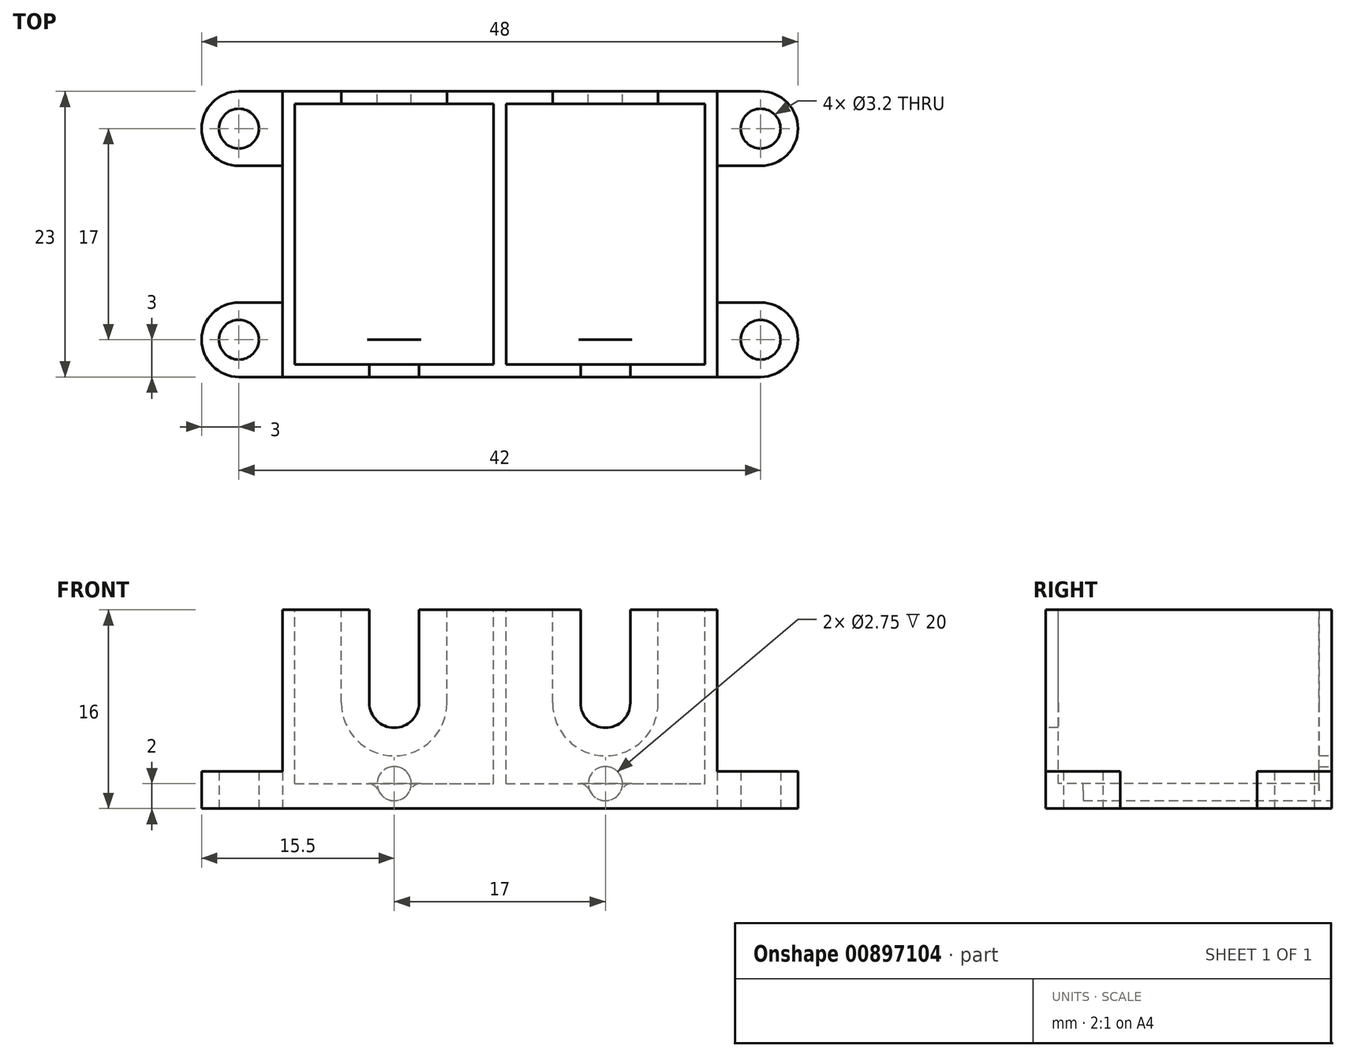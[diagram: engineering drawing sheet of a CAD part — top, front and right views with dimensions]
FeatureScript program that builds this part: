
annotation { "Feature Type Name" : "Feature", "Feature Type Description" : "" }
export const myFeature = defineFeature(function(context is Context, id is Id, definition is map)
    precondition{}
    {
        {
            var Q0;
            Q0=qCreatedBy(makeId("Top.planeOp"),FACE);
            var sketch = newSketch(context, id + "F0", { "sketchPlane" : qUnion([Q0])});
            skLineSegment(sketch, "E0.bottom", {"start": v(-17.5, 11.5) * mm, "end": v(17.5, 11.5) * mm});
            skLineSegment(sketch, "E0.top", {"start": v(-17.5, -11.5) * mm, "end": v(17.5, -11.5) * mm});
            skLineSegment(sketch, "E0.left", {"start": v(-17.5, 11.5) * mm, "end": v(-17.5, -11.5) * mm});
            skLineSegment(sketch, "E0.right", {"start": v(17.5, 11.5) * mm, "end": v(17.5, -11.5) * mm});
            skSolve(sketch);
        }
        {
            var Q0;
            Q0 = qSketchRegion(id + "F0", true);
            extrude(context, id + "F1", {"entities" : qUnion([Q0]), "depth" : 16 * mm, "offsetDistance" : 25 * mm});
        }
        {
            var Q0;
            Q0=makeQuery(id+"F1.opExtrude","CAP_FACE",FACE,{"disambiguationData":[OSD([sQuery(id+"F0.wireOp",EDGE,"E0.bottom"),sQuery(id+"F0.wireOp",EDGE,"E0.top"),sQuery(id+"F0.wireOp",EDGE,"E0.left"),sQuery(id+"F0.wireOp",EDGE,"E0.right")])],"isStart":false});
            var sketch = newSketch(context, id + "F2", { "sketchPlane" : qUnion([Q0])});
            skLineSegment(sketch, "E1.bottom", {"start": v(-16.5, 10.5) * mm, "end": v(-0.5, 10.5) * mm});
            skLineSegment(sketch, "E1.top", {"start": v(-16.5, -10.5) * mm, "end": v(-0.5, -10.5) * mm});
            skLineSegment(sketch, "E1.left", {"start": v(-16.5, 10.5) * mm, "end": v(-16.5, -10.5) * mm});
            skLineSegment(sketch, "E1.right", {"start": v(-0.5, 10.5) * mm, "end": v(-0.5, -10.5) * mm});
            skLineSegment(sketch, "E2.bottom", {"start": v(0.5, 10.5) * mm, "end": v(16.5, 10.5) * mm});
            skLineSegment(sketch, "E2.top", {"start": v(0.5, -10.5) * mm, "end": v(16.5, -10.5) * mm});
            skLineSegment(sketch, "E2.left", {"start": v(0.5, 10.5) * mm, "end": v(0.5, -10.5) * mm});
            skLineSegment(sketch, "E2.right", {"start": v(16.5, 10.5) * mm, "end": v(16.5, -10.5) * mm});
            skSolve(sketch);
        }
        {
            var Q0;
            Q0 = qSketchRegion(id + "F2", true);
            extrude(context, id + "F3", {"entities" : qUnion([Q0]), "operationType" : NewBodyOperationType.REMOVE, "oppositeDirection" : true, "depth" : 14 * mm, "offsetDistance" : 25 * mm});
        }
        {
            var Q0;
            Q0=makeQuery(id+"F1.opExtrude","SWEPT_FACE",FACE,{"disambiguationData":[OSD([sQuery(id+"F0.wireOp",EDGE,"E0.top")])]});
            var sketch = newSketch(context, id + "F4", { "sketchPlane" : qUnion([Q0])});
            skArc(sketch, "E3", {"start": v(-10.5, 8.5) * mm, "mid": v(-8.5, 6.5) * mm, "end": v(-6.5, 8.5) * mm});
            skArc(sketch, "E4", {"start": v(6.5, 8.5) * mm, "mid": v(8.5, 6.5) * mm, "end": v(10.5, 8.5) * mm});
            skLineSegment(sketch, "E5.top", {"start": v(-10.5, 16) * mm, "end": v(-6.5, 16) * mm});
            skLineSegment(sketch, "E5.left", {"start": v(-10.5, 8.5) * mm, "end": v(-10.5, 16) * mm});
            skLineSegment(sketch, "E5.right", {"start": v(-6.5, 8.5) * mm, "end": v(-6.5, 16) * mm});
            skLineSegment(sketch, "E6.top", {"start": v(6.5, 16) * mm, "end": v(10.5, 16) * mm});
            skLineSegment(sketch, "E6.left", {"start": v(6.5, 8.5) * mm, "end": v(6.5, 16) * mm});
            skLineSegment(sketch, "E6.right", {"start": v(10.5, 8.5) * mm, "end": v(10.5, 16) * mm});
            skSolve(sketch);
        }
        {
            var Q0;
            Q0 = qSketchRegion(id + "F4", true);
            extrude(context, id + "F5", {"entities" : qUnion([Q0]), "operationType" : NewBodyOperationType.REMOVE, "oppositeDirection" : true, "depth" : 25 * mm, "offsetDistance" : 25 * mm});
        }
        {
            var Q0;
            Q0=makeQuery(id+"F1.opExtrude","SWEPT_FACE",FACE,{"disambiguationData":[OSD([sQuery(id+"F0.wireOp",EDGE,"E0.bottom")])]});
            var sketch = newSketch(context, id + "F6", { "sketchPlane" : qUnion([Q0])});
            skArc(sketch, "E7", {"start": v(-12.75, 8.5) * mm, "mid": v(-8.5, 4.25) * mm, "end": v(-4.25, 8.5) * mm});
            skArc(sketch, "E8", {"start": v(4.25, 8.5) * mm, "mid": v(8.5, 4.25) * mm, "end": v(12.75, 8.5) * mm});
            skLineSegment(sketch, "E9", {"start": v(-12.75, 8.5) * mm, "end": v(-12.75, 16) * mm});
            skLineSegment(sketch, "E10", {"start": v(-4.25, 8.5) * mm, "end": v(-4.25, 16) * mm});
            skLineSegment(sketch, "E11", {"start": v(4.25, 8.5) * mm, "end": v(4.25, 16) * mm});
            skLineSegment(sketch, "E12", {"start": v(12.75, 8.5) * mm, "end": v(12.75, 16) * mm});
            skLineSegment(sketch, "E13", {"start": v(-12.75, 16) * mm, "end": v(-4.25, 16) * mm});
            skLineSegment(sketch, "E14", {"start": v(4.25, 16) * mm, "end": v(12.75, 16) * mm});
            skSolve(sketch);
        }
        {
            var Q0;
            Q0=makeQuery(id+"F6.imprint","IMPRINT",FACE,{"disambiguationData":[TD([[makeQuery(id+"F6.imprint","IMPRINT",EDGE,{"derivedFrom":sQuery(id+"F6.wireOp",EDGE,"E7")}),1.0]])]});
            var Q1;
            Q1=makeQuery(id+"F6.imprint","IMPRINT",FACE,{"disambiguationData":[TD([[makeQuery(id+"F6.imprint","IMPRINT",EDGE,{"derivedFrom":sQuery(id+"F6.wireOp",EDGE,"E8")}),1.0]])]});
            extrude(context, id + "F7", {"entities" : qUnion([Q0, Q1]), "operationType" : NewBodyOperationType.REMOVE, "oppositeDirection" : true, "depth" : 3 * mm, "offsetDistance" : 25 * mm});
        }
        {
            var Q0;
            Q0=makeQuery(id+"F1.opExtrude","SWEPT_FACE",FACE,{"disambiguationData":[OSD([sQuery(id+"F0.wireOp",EDGE,"E0.bottom")])]});
            var sketch = newSketch(context, id + "F8", { "sketchPlane" : qUnion([Q0])});
            skCircle(sketch, "E15", {"center": v(-8.5, 2) * mm, "radius": 1.38 * mm});
            skPoint(sketch, "E15.centerSnap0", {"position": v(-8.5, 4.25) * mm});
            skCircle(sketch, "E16", {"center": v(8.5, 2) * mm, "radius": 1.38 * mm});
            skPoint(sketch, "E16.centerSnap0", {"position": v(8.5, 4.25) * mm});
            skSolve(sketch);
        }
        {
            var Q0;
            Q0 = qSketchRegion(id + "F8", true);
            extrude(context, id + "F9", {"entities" : qUnion([Q0]), "operationType" : NewBodyOperationType.REMOVE, "oppositeDirection" : true, "depth" : 20 * mm, "offsetDistance" : 25 * mm});
        }
        {
            var Q0;
            Q0=makeQuery(id+"F9.boolean.opBoolean","INTERSECT",EDGE,{"disambiguationData":[OD(0.0)],"derivedFrom":[makeQuery(id+"F3.boolean.opBoolean","COPY",FACE,{"derivedFrom":makeQuery(id+"F3.opExtrude","CAP_FACE",FACE,{"disambiguationData":[OSD([sQuery(id+"F2.wireOp",EDGE,"E2.bottom"),sQuery(id+"F2.wireOp",EDGE,"E2.top"),sQuery(id+"F2.wireOp",EDGE,"E2.left"),sQuery(id+"F2.wireOp",EDGE,"E2.right")])],"isStart":false})}),makeQuery(id+"F9.opExtrude","SWEPT_FACE",FACE,{"disambiguationData":[OSD([sQuery(id+"F8.wireOp",EDGE,"E15")])]})]});
            var Q1;
            Q1=makeQuery(id+"F9.boolean.opBoolean","INTERSECT",EDGE,{"disambiguationData":[OD(1.0)],"derivedFrom":[makeQuery(id+"F3.boolean.opBoolean","COPY",FACE,{"derivedFrom":makeQuery(id+"F3.opExtrude","CAP_FACE",FACE,{"disambiguationData":[OSD([sQuery(id+"F2.wireOp",EDGE,"E2.bottom"),sQuery(id+"F2.wireOp",EDGE,"E2.top"),sQuery(id+"F2.wireOp",EDGE,"E2.left"),sQuery(id+"F2.wireOp",EDGE,"E2.right")])],"isStart":false})}),makeQuery(id+"F9.opExtrude","SWEPT_FACE",FACE,{"disambiguationData":[OSD([sQuery(id+"F8.wireOp",EDGE,"E15")])]})]});
            var Q2;
            Q2=makeQuery(id+"F9.boolean.opBoolean","INTERSECT",EDGE,{"disambiguationData":[OD(1.0)],"derivedFrom":[makeQuery(id+"F3.boolean.opBoolean","COPY",FACE,{"derivedFrom":makeQuery(id+"F3.opExtrude","CAP_FACE",FACE,{"disambiguationData":[OSD([sQuery(id+"F2.wireOp",EDGE,"E1.bottom"),sQuery(id+"F2.wireOp",EDGE,"E1.top"),sQuery(id+"F2.wireOp",EDGE,"E1.left"),sQuery(id+"F2.wireOp",EDGE,"E1.right")])],"isStart":false})}),makeQuery(id+"F9.opExtrude","SWEPT_FACE",FACE,{"disambiguationData":[OSD([sQuery(id+"F8.wireOp",EDGE,"E16")])]})]});
            var Q3;
            Q3=makeQuery(id+"F9.boolean.opBoolean","INTERSECT",EDGE,{"disambiguationData":[OD(0.0)],"derivedFrom":[makeQuery(id+"F3.boolean.opBoolean","COPY",FACE,{"derivedFrom":makeQuery(id+"F3.opExtrude","CAP_FACE",FACE,{"disambiguationData":[OSD([sQuery(id+"F2.wireOp",EDGE,"E1.bottom"),sQuery(id+"F2.wireOp",EDGE,"E1.top"),sQuery(id+"F2.wireOp",EDGE,"E1.left"),sQuery(id+"F2.wireOp",EDGE,"E1.right")])],"isStart":false})}),makeQuery(id+"F9.opExtrude","SWEPT_FACE",FACE,{"disambiguationData":[OSD([sQuery(id+"F8.wireOp",EDGE,"E16")])]})]});
            fillet(context, id + "F10", {"entities" : qUnion([Q0, Q1, Q2, Q3]), "radius" : 1 * mm, "tangentPropagation" : true, "allowEdgeOverflow" : false});
        }
        {
            var Q0;
            Q0=qCreatedBy(makeId("Top.planeOp"),FACE);
            var sketch = newSketch(context, id + "F11", { "sketchPlane" : qUnion([Q0])});
            skLineSegment(sketch, "E17.bottom", {"start": v(-17.5, 11.5) * mm, "end": v(-21, 11.5) * mm});
            skLineSegment(sketch, "E17.top", {"start": v(-17.5, 5.5) * mm, "end": v(-21, 5.5) * mm});
            skLineSegment(sketch, "E17.left", {"start": v(-17.5, 11.5) * mm, "end": v(-17.5, 5.5) * mm});
            skLineSegment(sketch, "E17.right", {"start": v(-21, 11.5) * mm, "end": v(-21, 5.5) * mm, "construction": true});
            skLineSegment(sketch, "E18.bottom", {"start": v(17.5, 11.5) * mm, "end": v(21, 11.5) * mm});
            skLineSegment(sketch, "E18.top", {"start": v(17.5, 5.5) * mm, "end": v(21, 5.5) * mm});
            skLineSegment(sketch, "E18.left", {"start": v(17.5, 11.5) * mm, "end": v(17.5, 5.5) * mm});
            skLineSegment(sketch, "E18.right", {"start": v(21, 11.5) * mm, "end": v(21, 5.5) * mm, "construction": true});
            skLineSegment(sketch, "E19.bottom", {"start": v(-17.5, -11.5) * mm, "end": v(-21, -11.5) * mm});
            skLineSegment(sketch, "E19.top", {"start": v(-17.5, -5.5) * mm, "end": v(-21, -5.5) * mm});
            skLineSegment(sketch, "E19.left", {"start": v(-17.5, -11.5) * mm, "end": v(-17.5, -5.5) * mm});
            skLineSegment(sketch, "E19.right", {"start": v(-21, -11.5) * mm, "end": v(-21, -5.5) * mm, "construction": true});
            skArc(sketch, "E20", {"start": v(21, 5.5) * mm, "mid": v(24, 8.5) * mm, "end": v(21, 11.5) * mm});
            skArc(sketch, "E21", {"start": v(-21, 11.5) * mm, "mid": v(-24, 8.5) * mm, "end": v(-21, 5.5) * mm});
            skArc(sketch, "E22", {"start": v(-21, -5.5) * mm, "mid": v(-24, -8.5) * mm, "end": v(-21, -11.5) * mm});
            skLineSegment(sketch, "E23.bottom", {"start": v(17.5, -5.5) * mm, "end": v(21, -5.5) * mm});
            skLineSegment(sketch, "E23.top", {"start": v(17.5, -11.5) * mm, "end": v(21, -11.5) * mm});
            skLineSegment(sketch, "E23.left", {"start": v(17.5, -5.5) * mm, "end": v(17.5, -11.5) * mm});
            skLineSegment(sketch, "E23.right", {"start": v(21, -5.5) * mm, "end": v(21, -11.5) * mm, "construction": true});
            skArc(sketch, "E24", {"start": v(21, -11.5) * mm, "mid": v(24, -8.5) * mm, "end": v(21, -5.5) * mm});
            skCircle(sketch, "E25", {"center": v(21, 8.5) * mm, "radius": 1.6 * mm});
            skCircle(sketch, "E26", {"center": v(-21, 8.5) * mm, "radius": 1.6 * mm});
            skCircle(sketch, "E27", {"center": v(21, -8.5) * mm, "radius": 1.6 * mm});
            skCircle(sketch, "E28", {"center": v(-21, -8.5) * mm, "radius": 1.6 * mm});
            skSolve(sketch);
        }
        {
            var Q0;
            Q0 = qSketchRegion(id + "F11", true);
            extrude(context, id + "F12", {"entities" : qUnion([Q0]), "operationType" : NewBodyOperationType.ADD, "depth" : 3 * mm, "offsetDistance" : 25 * mm});
        }
    });
